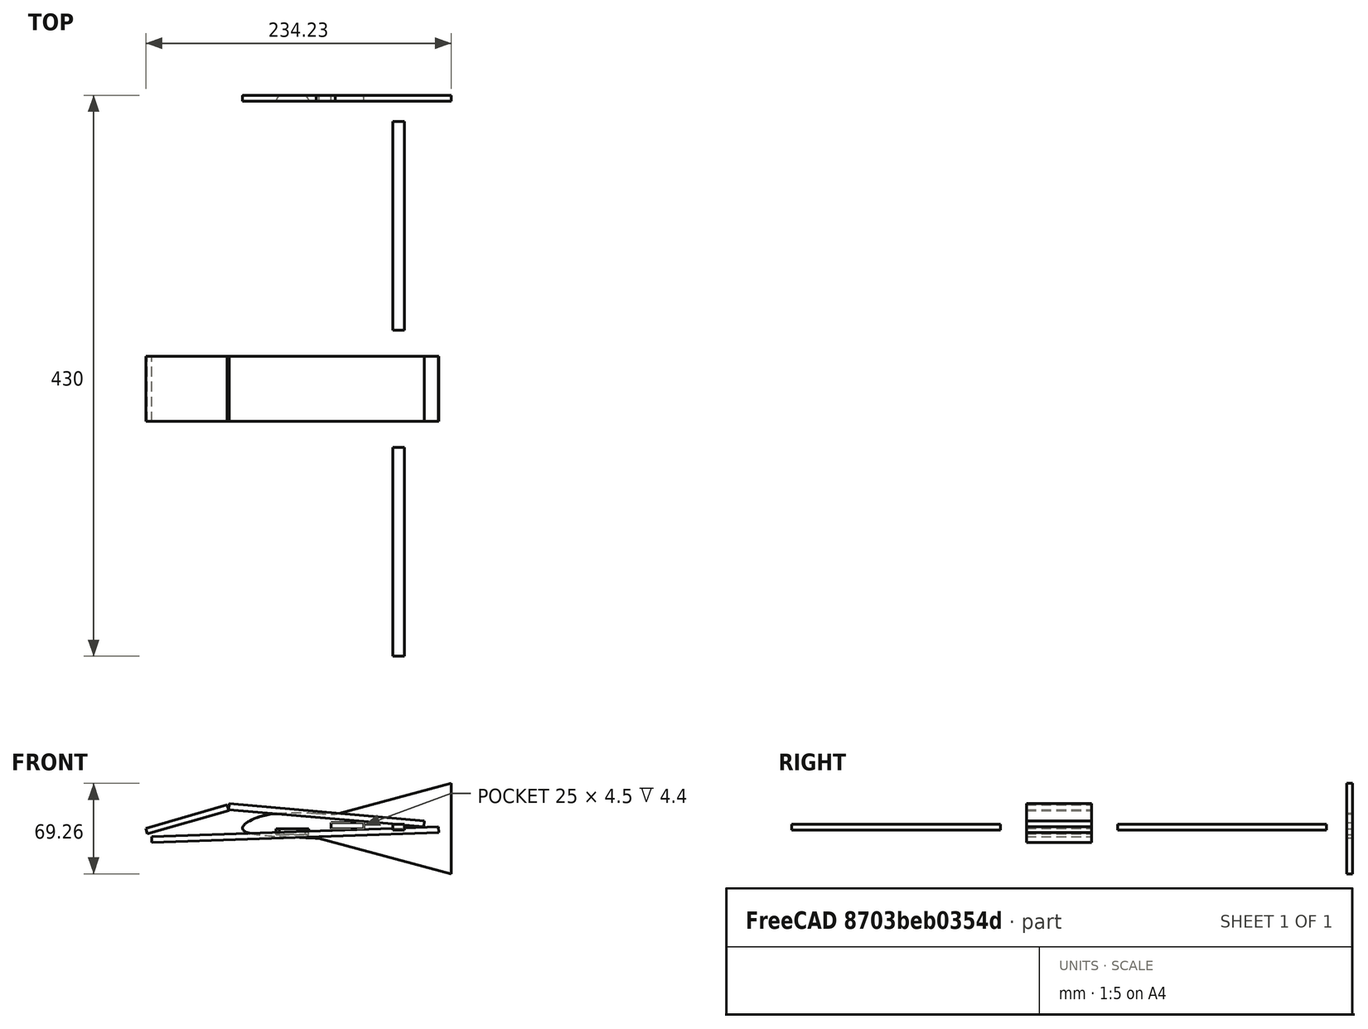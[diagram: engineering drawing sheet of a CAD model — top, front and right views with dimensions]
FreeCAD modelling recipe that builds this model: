
FCSTD DOCUMENT  (FreeCAD 0.21R33694 (Git))
Label: wingtest4
License: All rights reserved
LicenseURL: http://en.wikipedia.org/wiki/All_rights_reserved
objects: Part::FeaturePython×110, Part::Part2DObjectPython×22, Part::Box×9, Part::Cut×9, PartDesign::Body×8, Sketcher::SketchObject×6, PartDesign::FeatureBase×4, PartDesign::Pad×3, App::DocumentObjectGroup×3, Part::RuledSurface×2, Spreadsheet::Sheet×1, Part::Cylinder×1, Part::Fuse×1, App::FeaturePython×1, App::MeasureDistance×1, Part::MultiFuse×1, Mesh::Feature×1, Part::Feature×1
note: 181 computed .brp shape members not serialized (recipe doc carries the construction recipe); baked Part::Feature solids carry a one-line shape summary decoded from their .brp

FEATURE [Part::FeaturePython] wrib  # WARN: FeaturePython — macro-defined, semantics opaque (R4)
  Chord = 250
  Coordinates = (101) [(1,0,-1.66492e-17),(0.99901,0,0.000165389),(0.996045,0,0.000659808),(0.991115,0,0.00147806),(0.984241,0,0.00261162),(0.97545,0,0.00404888),+95 more]
  NacaNbrPoint = 50
  NacaProfil = 24112
  RibProfil = 24112
  Thickness = 0
  finite_TE = false
  splitSpline = true
  useSpline = true
  wingkey = 0
  expr: .Placement.Base.y = Spreadsheet.lw_start
FEATURE [Part::FeaturePython] wrib001  # WARN: FeaturePython — macro-defined, semantics opaque (R4)
  Chord = 250
  Coordinates = (101) [(1,0,-1.66492e-17),(0.99901,0,0.000165389),(0.996045,0,0.000659808),(0.991115,0,0.00147806),(0.984241,0,0.00261162),(0.97545,0,0.00404888),+95 more]
  NacaNbrPoint = 50
  NacaProfil = 24112
  Placement = pos=(0,50,0) rot=(1,0,0;0rad)
  RibProfil = 24112
  Thickness = 0
  finite_TE = false
  splitSpline = true
  useSpline = true
  wingkey = 0
  expr: .Placement.Base.y = Spreadsheet.rw_start
FEATURE [Part::FeaturePython] wrib002  # WARN: FeaturePython — macro-defined, semantics opaque (R4)
  Chord = 250
  Coordinates = (101) [(1,0,-1.66492e-17),(0.99901,0,0.000165389),(0.996045,0,0.000659808),(0.991115,0,0.00147806),(0.984241,0,0.00261162),(0.97545,0,0.00404888),+95 more]
  NacaNbrPoint = 50
  NacaProfil = 24112
  Placement = pos=(0,-40,0) rot=(1,0,0;0rad)
  RibProfil = 24112
  Thickness = 0
  finite_TE = false
  splitSpline = true
  useSpline = true
  wingkey = 0
  expr: .Placement.Base.y = Spreadsheet.lw_start - Spreadsheet.spacing * 2
FEATURE [Part::FeaturePython] wrib003  # WARN: FeaturePython — macro-defined, semantics opaque (R4)
  Chord = 250
  Coordinates = (101) [(1,0,-1.66492e-17),(0.99901,0,0.000165389),(0.996045,0,0.000659808),(0.991115,0,0.00147806),(0.984241,0,0.00261162),(0.97545,0,0.00404888),+95 more]
  NacaNbrPoint = 50
  NacaProfil = 24112
  Placement = pos=(0,-20,0) rot=(1,0,0;0rad)
  RibProfil = 24112
  Thickness = 0
  finite_TE = false
  splitSpline = true
  useSpline = true
  wingkey = 0
  expr: .Placement.Base.y = <<sht>>.lw_start - <<sht>>.spacing
FEATURE [Part::FeaturePython] wrib004  # WARN: FeaturePython — macro-defined, semantics opaque (R4)
  Chord = 250
  Coordinates = (101) [(1,0,-1.66492e-17),(0.99901,0,0.000165389),(0.996045,0,0.000659808),(0.991115,0,0.00147806),(0.984241,0,0.00261162),(0.97545,0,0.00404888),+95 more]
  NacaNbrPoint = 50
  NacaProfil = 24112
  Placement = pos=(0,70,0) rot=(1,0,0;0rad)
  RibProfil = 24112
  Thickness = 0
  finite_TE = false
  splitSpline = true
  useSpline = true
  wingkey = 0
  expr: .Placement.Base.y = Spreadsheet.rw_start + Spreadsheet.spacing
FEATURE [Part::FeaturePython] wrib005  # WARN: FeaturePython — macro-defined, semantics opaque (R4)
  Chord = 250
  Coordinates = (101) [(1,0,-1.66492e-17),(0.99901,0,0.000165389),(0.996045,0,0.000659808),(0.991115,0,0.00147806),(0.984241,0,0.00261162),(0.97545,0,0.00404888),+95 more]
  NacaNbrPoint = 50
  NacaProfil = 24112
  Placement = pos=(0,90,0) rot=(1,0,0;0rad)
  RibProfil = 24112
  Thickness = 0
  finite_TE = false
  splitSpline = true
  useSpline = true
  wingkey = 0
  expr: .Placement.Base.y = <<sht>>.rw_start + <<sht>>.spacing * 2
FEATURE [Spreadsheet::Sheet] Spreadsheet  label="sht"
  cells = A1='spacing; B1(spacing)=20; A2='lw_start; B2(lw_start)=0; A3='rw_start; B3(rw_start)=50; A4='wing_step; B4(wing_step)=15; A5='fb_spacing; B5(fb_spacing)=15; A6='thickness; B6(thickness)=4.5
FEATURE [Part::FeaturePython] wrib006  # WARN: FeaturePython — macro-defined, semantics opaque (R4)
  Chord = 235
  Coordinates = (101) [(1,0,-1.66492e-17),(0.99901,0,0.000165389),(0.996045,0,0.000659808),(0.991115,0,0.00147806),(0.984241,0,0.00261162),(0.97545,0,0.00404888),+95 more]
  NacaNbrPoint = 50
  NacaProfil = 24112
  Placement = pos=(15,-60,0) rot=(1,0,0;0rad)
  RibProfil = 24112
  Thickness = 0
  finite_TE = false
  splitSpline = true
  useSpline = true
  wingkey = 0
  expr: .Placement.Base.x = <<sht>>.fb_spacing
  expr: .Placement.Base.y = <<sht>>.lw_start - <<sht>>.spacing * 3
FEATURE [Part::FeaturePython] wrib007  # WARN: FeaturePython — macro-defined, semantics opaque (R4)
  Chord = 235
  Coordinates = (101) [(1,0,-1.66492e-17),(0.99901,0,0.000165389),(0.996045,0,0.000659808),(0.991115,0,0.00147806),(0.984241,0,0.00261162),(0.97545,0,0.00404888),+95 more]
  NacaNbrPoint = 50
  NacaProfil = 24112
  Placement = pos=(15,110,0) rot=(1,0,0;0rad)
  RibProfil = 24112
  Thickness = 0
  finite_TE = false
  splitSpline = true
  useSpline = true
  wingkey = 0
  expr: .Placement.Base.x = <<sht>>.fb_spacing
  expr: .Placement.Base.y = <<sht>>.rw_start + 3 * <<sht>>.spacing
FEATURE [Part::FeaturePython] wrib008  # WARN: FeaturePython — macro-defined, semantics opaque (R4)
  Chord = 220
  Coordinates = (101) [(1,0,-1.66492e-17),(0.99901,0,0.000165389),(0.996045,0,0.000659808),(0.991115,0,0.00147806),(0.984241,0,0.00261162),(0.97545,0,0.00404888),+95 more]
  NacaNbrPoint = 50
  NacaProfil = 24112
  Placement = pos=(30,-80,0) rot=(1,0,0;0rad)
  RibProfil = 24112
  Thickness = 0
  finite_TE = false
  splitSpline = true
  useSpline = true
  wingkey = 0
  expr: .Placement.Base.x = <<sht>>.fb_spacing * 2
  expr: .Placement.Base.y = <<sht>>.lw_start - <<sht>>.spacing * 4
FEATURE [Part::FeaturePython] wrib009  # WARN: FeaturePython — macro-defined, semantics opaque (R4)
  Chord = 220
  Coordinates = (101) [(1,0,-1.66492e-17),(0.99901,0,0.000165389),(0.996045,0,0.000659808),(0.991115,0,0.00147806),(0.984241,0,0.00261162),(0.97545,0,0.00404888),+95 more]
  NacaNbrPoint = 50
  NacaProfil = 24112
  Placement = pos=(30,130,0) rot=(1,0,0;0rad)
  RibProfil = 24112
  Thickness = 0
  finite_TE = false
  splitSpline = true
  useSpline = true
  wingkey = 0
  expr: .Placement.Base.x = <<sht>>.fb_spacing * 2
  expr: .Placement.Base.y = <<sht>>.rw_start + <<sht>>.spacing * 4
FEATURE [Part::FeaturePython] wrib010  # WARN: FeaturePython — macro-defined, semantics opaque (R4)
  Chord = 205
  Coordinates = (101) [(1,0,-1.66492e-17),(0.99901,0,0.000165389),(0.996045,0,0.000659808),(0.991115,0,0.00147806),(0.984241,0,0.00261162),(0.97545,0,0.00404888),+95 more]
  NacaNbrPoint = 50
  NacaProfil = 24112
  Placement = pos=(45,-100,0) rot=(1,0,0;0rad)
  RibProfil = 24112
  Thickness = 0
  finite_TE = false
  splitSpline = true
  useSpline = true
  wingkey = 0
  expr: .Placement.Base.x = <<sht>>.fb_spacing * 3
  expr: .Placement.Base.y = <<sht>>.lw_start - <<sht>>.spacing * 5
FEATURE [Part::FeaturePython] wrib011  # WARN: FeaturePython — macro-defined, semantics opaque (R4)
  Chord = 190
  Coordinates = (101) [(1,0,-1.66492e-17),(0.99901,0,0.000165389),(0.996045,0,0.000659808),(0.991115,0,0.00147806),(0.984241,0,0.00261162),(0.97545,0,0.00404888),+95 more]
  NacaNbrPoint = 50
  NacaProfil = 24112
  Placement = pos=(60,-120,0) rot=(1,0,0;0rad)
  RibProfil = 24112
  Thickness = 0
  finite_TE = false
  splitSpline = true
  useSpline = true
  wingkey = 0
  expr: .Placement.Base.x = <<sht>>.fb_spacing * 4
  expr: .Placement.Base.y = <<sht>>.lw_start - <<sht>>.spacing * 6
FEATURE [Part::FeaturePython] wrib012  # WARN: FeaturePython — macro-defined, semantics opaque (R4)
  Chord = 190
  Coordinates = (101) [(1,0,-1.66492e-17),(0.99901,0,0.000165389),(0.996045,0,0.000659808),(0.991115,0,0.00147806),(0.984241,0,0.00261162),(0.97545,0,0.00404888),+95 more]
  NacaNbrPoint = 50
  NacaProfil = 24112
  Placement = pos=(60,170,0) rot=(1,0,0;0rad)
  RibProfil = 24112
  Thickness = 0
  finite_TE = false
  splitSpline = true
  useSpline = true
  wingkey = 0
  expr: .Placement.Base.x = <<sht>>.fb_spacing * 4
  expr: .Placement.Base.y = <<sht>>.rw_start + <<sht>>.spacing * 6
FEATURE [Part::FeaturePython] wrib013  # WARN: FeaturePython — macro-defined, semantics opaque (R4)
  Chord = 205
  Coordinates = (101) [(1,0,-1.66492e-17),(0.99901,0,0.000165389),(0.996045,0,0.000659808),(0.991115,0,0.00147806),(0.984241,0,0.00261162),(0.97545,0,0.00404888),+95 more]
  NacaNbrPoint = 50
  NacaProfil = 24112
  Placement = pos=(45,150,0) rot=(1,0,0;0rad)
  RibProfil = 24112
  Thickness = 0
  finite_TE = false
  splitSpline = true
  useSpline = true
  wingkey = 0
  expr: .Placement.Base.x = <<sht>>.fb_spacing * 3
  expr: .Placement.Base.y = <<sht>>.rw_start + <<sht>>.spacing * 5
FEATURE [Part::FeaturePython] wrib014  # WARN: FeaturePython — macro-defined, semantics opaque (R4)
  Chord = 175
  Coordinates = (101) [(1,0,-1.66492e-17),(0.99901,0,0.000165389),(0.996045,0,0.000659808),(0.991115,0,0.00147806),(0.984241,0,0.00261162),(0.97545,0,0.00404888),+95 more]
  NacaNbrPoint = 50
  NacaProfil = 24112
  Placement = pos=(75,-140,0) rot=(1,0,0;0rad)
  RibProfil = 24112
  Thickness = 0
  finite_TE = false
  splitSpline = true
  useSpline = true
  wingkey = 0
  expr: .Placement.Base.x = <<sht>>.fb_spacing * 5
  expr: .Placement.Base.y = <<sht>>.lw_start - <<sht>>.spacing * 7
FEATURE [Part::FeaturePython] wrib015  # WARN: FeaturePython — macro-defined, semantics opaque (R4)
  Chord = 175
  Coordinates = (101) [(1,0,-1.66492e-17),(0.99901,0,0.000165389),(0.996045,0,0.000659808),(0.991115,0,0.00147806),(0.984241,0,0.00261162),(0.97545,0,0.00404888),+95 more]
  NacaNbrPoint = 50
  NacaProfil = 24112
  Placement = pos=(75,190,0) rot=(1,0,0;0rad)
  RibProfil = 24112
  Thickness = 0
  finite_TE = false
  splitSpline = true
  useSpline = true
  wingkey = 0
  expr: .Placement.Base.x = <<sht>>.fb_spacing * 5
  expr: .Placement.Base.y = <<sht>>.rw_start + <<sht>>.spacing * 7
FEATURE [Part::FeaturePython] wrib016  # WARN: FeaturePython — macro-defined, semantics opaque (R4)
  Chord = 160
  Coordinates = (101) [(1,0,-1.65073e-17),(0.999032,0,0.000273506),(0.996132,0,0.00109061),(0.99131,0,0.00244114),(0.984583,0,0.00430839),(0.975972,0,0.00666943),+95 more]
  NacaNbrPoint = 50
  NacaProfil = 4412
  Placement = pos=(90,210,0) rot=(1,0,0;0rad)
  RibProfil = 4412
  Thickness = 0
  finite_TE = false
  splitSpline = true
  useSpline = true
  wingkey = 0
  expr: .Placement.Base.x = <<sht>>.fb_spacing * 6
  expr: .Placement.Base.y = <<sht>>.rw_start + <<sht>>.spacing * 8
FEATURE [Part::FeaturePython] wrib017  # WARN: FeaturePython — macro-defined, semantics opaque (R4)
  Chord = 160
  Coordinates = (101) [(1,0,-1.66492e-17),(0.99901,0,0.000165389),(0.996045,0,0.000659808),(0.991115,0,0.00147806),(0.984241,0,0.00261162),(0.97545,0,0.00404888),+95 more]
  NacaNbrPoint = 50
  NacaProfil = 24112
  Placement = pos=(90,-160,0) rot=(1,0,0;0rad)
  RibProfil = 24112
  Thickness = 0
  finite_TE = false
  splitSpline = true
  useSpline = true
  wingkey = 0
  expr: .Placement.Base.x = <<sht>>.fb_spacing * 6
  expr: .Placement.Base.y = <<sht>>.lw_start - <<sht>>.spacing * 8
FEATURE [Part::FeaturePython] wrib018  # WARN: FeaturePython — macro-defined, semantics opaque (R4)
  Chord = 160
  Coordinates = (101) [(1,0,-1.66492e-17),(0.99901,0,0.000165389),(0.996045,0,0.000659808),(0.991115,0,0.00147806),(0.984241,0,0.00261162),(0.97545,0,0.00404888),+95 more]
  NacaNbrPoint = 50
  NacaProfil = 24112
  Placement = pos=(90,-180,0) rot=(1,0,0;0rad)
  RibProfil = 24112
  Thickness = 0
  finite_TE = false
  splitSpline = true
  useSpline = true
  wingkey = 0
  expr: .Placement.Base.x = <<sht>>.fb_spacing * 6
  expr: .Placement.Base.y = <<sht>>.lw_start - <<sht>>.spacing * 9
FEATURE [Part::FeaturePython] wrib019  # WARN: FeaturePython — macro-defined, semantics opaque (R4)
  Chord = 160
  Coordinates = (101) [(1,0,-1.66492e-17),(0.99901,0,0.000165389),(0.996045,0,0.000659808),(0.991115,0,0.00147806),(0.984241,0,0.00261162),(0.97545,0,0.00404888),+95 more]
  NacaNbrPoint = 50
  NacaProfil = 24112
  Placement = pos=(90,-200,0) rot=(1,0,0;0rad)
  RibProfil = 24112
  Thickness = 0
  finite_TE = false
  splitSpline = true
  useSpline = true
  wingkey = 0
  expr: .Placement.Base.x = <<sht>>.fb_spacing * 6
  expr: .Placement.Base.y = <<sht>>.lw_start - <<sht>>.spacing * 10
FEATURE [Part::FeaturePython] wrib020  # WARN: FeaturePython — macro-defined, semantics opaque (R4)
  Chord = 160
  Coordinates = (101) [(1,0,-1.66492e-17),(0.99901,0,0.000165389),(0.996045,0,0.000659808),(0.991115,0,0.00147806),(0.984241,0,0.00261162),(0.97545,0,0.00404888),+95 more]
  NacaNbrPoint = 50
  NacaProfil = 24112
  Placement = pos=(90,230,0) rot=(1,0,0;0rad)
  RibProfil = 24112
  Thickness = 0
  finite_TE = false
  splitSpline = true
  useSpline = true
  wingkey = 0
  expr: .Placement.Base.x = <<sht>>.fb_spacing * 6
  expr: .Placement.Base.y = <<sht>>.rw_start + <<sht>>.spacing * 9
FEATURE [Part::FeaturePython] wrib021  # WARN: FeaturePython — macro-defined, semantics opaque (R4)
  Chord = 160
  Coordinates = (101) [(1,0,-1.66492e-17),(0.99901,0,0.000165389),(0.996045,0,0.000659808),(0.991115,0,0.00147806),(0.984241,0,0.00261162),(0.97545,0,0.00404888),+95 more]
  NacaNbrPoint = 50
  NacaProfil = 24112
  Placement = pos=(90,250,0) rot=(1,0,0;0rad)
  RibProfil = 24112
  Thickness = 0
  finite_TE = false
  splitSpline = true
  useSpline = true
  wingkey = 0
  expr: .Placement.Base.x = <<sht>>.fb_spacing * 6
  expr: .Placement.Base.y = <<sht>>.rw_start + <<sht>>.spacing * 10
FEATURE [Sketcher::SketchObject] Sketch
  FullyConstrained = false
  MapMode = 5
  Placement = pos=(0,0,0) rot=(1,0,0;1.5708rad)
  Support = -> [XZ_Plane]
  sketch-geometry (29):
    g0: LineSegment StartX=0 StartY=34.6308 StartZ=0 EndX=0 EndY=-34.6308 EndZ=0
    g1: LineSegment StartX=0 StartY=-34.6308 StartZ=0 EndX=-101.691 EndY=-7.38276 EndZ=0
    g2-g12: Circle x11 (B-spline internal-alignment scaffolding for g13; pole/knot coordinates omitted)
    g13: BSplineCurve PolesCount=11 KnotsCount=9 Degree=3 IsPeriodic=0
    g14: GeomPoint X=-103.524 Y=11.6623 Z=0
    g15: GeomPoint X=-140.833 Y=10.5678 Z=0
    g16: GeomPoint X=-152.621 Y=6.9811 Z=0
    g17: GeomPoint X=-158.306 Y=3.35011 Z=0
    g18: GeomPoint X=-160.007 Y=0.321331 Z=0
    g19: GeomPoint X=-158.483 Y=-2.12294 Z=0
    g20: GeomPoint X=-153.453 Y=-3.75246 Z=0
    g21: GeomPoint X=-144.695 Y=-5.06316 Z=0
    g22: GeomPoint X=-101.691 Y=-7.38276 Z=0
    g23: LineSegment StartX=-88.9876 StartY=10.9761 StartZ=0 EndX=0 EndY=34.6308 EndZ=0
    g24: Circle CenterX=-103.524 CenterY=11.6623 CenterZ=0 NormalX=0 NormalY=0 NormalZ=1 AngleXU=0 Radius=1
    g25: Circle CenterX=-88.9876 CenterY=10.9761 CenterZ=0 NormalX=0 NormalY=0 NormalZ=1 AngleXU=0 Radius=1
    g26: BSplineCurve PolesCount=2 KnotsCount=2 Degree=1 IsPeriodic=0
    g27: GeomPoint X=-103.524 Y=11.6623 Z=0
    g28: GeomPoint X=-88.9876 Y=10.9761 Z=0
  constraints (8):
    c: PointOnObject(g0,g-2)
    c: Coincident(g0,g1)
    c: Coincident(g23,g0)
    c: Symmetric(g0,g0,g-1)
    c: Weight(g2) = 1
    c: Equal(g2, g3-g12) x10
    c: Coincident(g13,g1)
    c: InternalAlignment(g2-g12 -> g13) x11
FEATURE [PartDesign::Pad] Pad
  Direction = (0,-1,2e-16)
  Length = 4.5
  Length2 = 10
  Placement = pos=(0,0,0) rot=(1,0,0;1.5708rad)
  Profile = -> Sketch
  ReferenceAxis = -> Sketch [N_Axis]
  Type = 0
  expr: Length = <<sht>>.thickness
FEATURE [PartDesign::Body] Body  label="wingtip1"
  Group = -> [Sketch,Pad]
  Origin = -> Origin
  Placement = pos=(250,250,0) rot=(0,0,1;0rad)
  Tip = -> Pad
  expr: .Placement.Base.x = <<sht>>.fb_spacing * 6 mm + wrib021.Chord
FEATURE [PartDesign::FeatureBase] Clone
  BaseFeature = -> Body
  Placement = pos=(250,250,0) rot=(0,0,1;0rad)
FEATURE [PartDesign::Body] Body001  label="wingtip2"
  BaseFeature = -> Body
  Group = -> [Clone]
  Origin = -> Origin001
  Placement = pos=(0,-449.2,0) rot=(0,0,1;0rad)
  Tip = -> Clone
  expr: .Placement.Base.y = 0
FEATURE [Sketcher::SketchObject] Sketch001
  FullyConstrained = false
  MapMode = 5
  Support = -> [XY_Plane002]
  sketch-geometry (51):
    g0-g25: Circle x26 (B-spline internal-alignment scaffolding for g26; pole/knot coordinates omitted)
    g26: BSplineCurve PolesCount=26 KnotsCount=24 Degree=3 IsPeriodic=0
    g27-g50: GeomPoint x24 (B-spline internal-alignment scaffolding for g26; pole/knot coordinates omitted)
  constraints (5):
    c: Weight(g0) = 1
    c: Equal(g0, g1-g25) x25
    c: Coincident(g26,g0)
    c: InternalAlignment(g0-g25 -> g26) x26
    c: InternalAlignment(g27-g50 -> g26) x24
FEATURE [PartDesign::Pad] Pad001
  Direction = (0,0,1)
  Length = 4.5
  Length2 = 10
  Profile = -> Sketch001
  ReferenceAxis = -> Sketch001 [N_Axis]
  Type = 0
  expr: Length = <<sht>>.thickness
FEATURE [PartDesign::Body] Body002  label="flexspar"
  Group = -> [Sketch001,Pad001]
  Origin = -> Origin002
  Tip = -> Pad001
FEATURE [PartDesign::FeatureBase] Clone001
  BaseFeature = -> Body002
FEATURE [PartDesign::Body] Body003
  BaseFeature = -> Body002
  Group = -> [Clone001]
  Origin = -> Origin003
  Placement = pos=(0,46.93,1e-15) rot=(1,0,0;3.14159rad)
  Tip = -> Clone001
FEATURE [Part::Box] Box  label="Cube"
  AttacherType = Attacher::AttachEngine3D
  Height = 20
  Length = 45
  Placement = pos=(210,-170,-9) rot=(0,0,1;0rad)
  Width = 141
  expr: .Placement.Base.x = 210
FEATURE [Part::FeaturePython] BooleanFragments  # WARN: FeaturePython — macro-defined, semantics opaque (R4)
  Mode = 0
  Objects = -> [wrib,wrib001,wrib002,wrib003,wrib004,wrib005,wrib006,wrib007,wrib008,wrib009,wrib010,wrib011,wrib012,wrib013,wrib014,wrib015,wrib016,wrib017,wrib018,wrib019,wrib020,wrib021,Body,Body001]
  Tolerance = 0
FEATURE [Part::Cylinder] Cylinder
  Angle = 360
  AttacherType = Attacher::AttachEngine3D
  FirstAngle = 0
  Height = 140
  Placement = pos=(210,-30,0.03) rot=(0.999938,0,0.01111;1.5708rad)
  Radius = 11
  SecondAngle = 0
FEATURE [Part::Fuse] Fusion
  Base = -> Box
  Tool = -> Cylinder
FEATURE [PartDesign::FeatureBase] Clone002
  BaseFeature = -> Fusion
FEATURE [PartDesign::Body] Body004
  BaseFeature = -> Fusion
  Group = -> [Clone002]
  Origin = -> Origin004
  Placement = pos=(0,253.5,0) rot=(0,0,1;0rad)
  Tip = -> Clone002
FEATURE [Part::FeaturePython] BooleanFragments001  # WARN: FeaturePython — macro-defined, semantics opaque (R4)
  Mode = 0
  Objects = -> [Body004,Fusion]
  Tolerance = 0
FEATURE [Part::Box] Box001  label="Cube001"
  AttacherType = Attacher::AttachEngine3D
  Height = 100
  Length = 340
  Placement = pos=(-1,-260,-49) rot=(0,0,1;0rad)
  Width = 550
FEATURE [Part::FeaturePython] BooleanFragments001_child0  label="BooleanFragments001.0"  # WARN: FeaturePython — macro-defined, semantics opaque (R4)
  Base = -> BooleanFragments001
  FilterType = 1
  Invert = false
  OverrideMaxVal = 0
  WindowFrom = 80
  WindowTo = 100
  items = 0
FEATURE [Part::FeaturePython] BooleanFragments001_child1  label="BooleanFragments001.1"  # WARN: FeaturePython — macro-defined, semantics opaque (R4)
  Base = -> BooleanFragments001
  FilterType = 1
  Invert = false
  OverrideMaxVal = 0
  WindowFrom = 80
  WindowTo = 100
  items = 1
FEATURE [Sketcher::SketchObject] Sketch002
  FullyConstrained = false
  MapMode = 5
  Placement = pos=(0,0,0) rot=(1,0,0;1.5708rad)
  Support = -> [XZ_Plane005]
  sketch-geometry (29):
    g0: LineSegment StartX=0 StartY=34.6308 StartZ=0 EndX=0 EndY=-34.6308 EndZ=0
    g1: LineSegment StartX=0 StartY=-34.6308 StartZ=0 EndX=-101.691 EndY=-7.38276 EndZ=0
    g2-g12: Circle x11 (B-spline internal-alignment scaffolding for g13; pole/knot coordinates omitted)
    g13: BSplineCurve PolesCount=11 KnotsCount=9 Degree=3 IsPeriodic=0
    g14: GeomPoint X=-103.524 Y=11.6623 Z=0
    g15: GeomPoint X=-140.833 Y=10.5678 Z=0
    g16: GeomPoint X=-152.621 Y=6.9811 Z=0
    g17: GeomPoint X=-158.306 Y=3.35011 Z=0
    g18: GeomPoint X=-160.007 Y=0.321331 Z=0
    g19: GeomPoint X=-158.483 Y=-2.12294 Z=0
    g20: GeomPoint X=-153.453 Y=-3.75246 Z=0
    g21: GeomPoint X=-144.695 Y=-5.06316 Z=0
    g22: GeomPoint X=-101.691 Y=-7.38276 Z=0
    g23: LineSegment StartX=-88.9876 StartY=10.9761 StartZ=0 EndX=0 EndY=34.6308 EndZ=0
    g24: Circle CenterX=-103.524 CenterY=11.6623 CenterZ=0 NormalX=0 NormalY=0 NormalZ=1 AngleXU=0 Radius=1
    g25: Circle CenterX=-88.9876 CenterY=10.9761 CenterZ=0 NormalX=0 NormalY=0 NormalZ=1 AngleXU=0 Radius=1
    g26: BSplineCurve PolesCount=2 KnotsCount=2 Degree=1 IsPeriodic=0
    g27: GeomPoint X=-103.524 Y=11.6623 Z=0
    g28: GeomPoint X=-88.9876 Y=10.9761 Z=0
  constraints (8):
    c: PointOnObject(g0,g-2)
    c: Coincident(g0,g1)
    c: Coincident(g23,g0)
    c: Symmetric(g0,g0,g-1)
    c: Weight(g2) = 1
    c: Equal(g2, g3-g12) x10
    c: Coincident(g13,g1)
    c: InternalAlignment(g2-g12 -> g13) x11
FEATURE [PartDesign::Pad] Pad002
  Direction = (0,-1,2e-16)
  Length = 4.5
  Length2 = 10
  Placement = pos=(0,0,0) rot=(1,0,0;1.5708rad)
  Profile = -> Sketch002
  ReferenceAxis = -> Sketch002 [N_Axis]
  Type = 0
  expr: Length = <<sht>>.thickness
FEATURE [PartDesign::Body] Body005  label="wingtip003"
  Group = -> [Sketch002,Pad002]
  Origin = -> Origin005
  Placement = pos=(250,250,0) rot=(0,0,1;0rad)
  Tip = -> Pad002
  expr: .Placement.Base.x = <<sht>>.fb_spacing * 6 mm + wrib043.Chord
FEATURE [PartDesign::FeatureBase] Clone003
  BaseFeature = -> Body005
  Placement = pos=(250,250,0) rot=(0,0,1;0rad)
FEATURE [PartDesign::Body] Body006  label="wingtip004"
  BaseFeature = -> Body005
  Group = -> [Clone003]
  Origin = -> Origin006
  Placement = pos=(0,-449.2,0) rot=(0,0,1;0rad)
  Tip = -> Clone003
  expr: .Placement.Base.y = 0
FEATURE [Part::FeaturePython] wrib022  # WARN: FeaturePython — macro-defined, semantics opaque (R4)
  Chord = 250
  Coordinates = (101) [(1,0,-1.66492e-17),(0.99901,0,0.000165389),(0.996045,0,0.000659808),(0.991115,0,0.00147806),(0.984241,0,0.00261162),(0.97545,0,0.00404888),+95 more]
  NacaNbrPoint = 50
  NacaProfil = 24112
  RibProfil = 24112
  Thickness = 0
  finite_TE = false
  splitSpline = true
  useSpline = true
  wingkey = 0
  expr: .Placement.Base.y = Spreadsheet.lw_start
FEATURE [Part::FeaturePython] wrib023  # WARN: FeaturePython — macro-defined, semantics opaque (R4)
  Chord = 250
  Coordinates = (101) [(1,0,-1.66492e-17),(0.99901,0,0.000165389),(0.996045,0,0.000659808),(0.991115,0,0.00147806),(0.984241,0,0.00261162),(0.97545,0,0.00404888),+95 more]
  NacaNbrPoint = 50
  NacaProfil = 24112
  Placement = pos=(0,50,0) rot=(1,0,0;0rad)
  RibProfil = 24112
  Thickness = 0
  finite_TE = false
  splitSpline = true
  useSpline = true
  wingkey = 0
  expr: .Placement.Base.y = Spreadsheet.rw_start
FEATURE [Part::FeaturePython] wrib024  # WARN: FeaturePython — macro-defined, semantics opaque (R4)
  Chord = 250
  Coordinates = (101) [(1,0,-1.66492e-17),(0.99901,0,0.000165389),(0.996045,0,0.000659808),(0.991115,0,0.00147806),(0.984241,0,0.00261162),(0.97545,0,0.00404888),+95 more]
  NacaNbrPoint = 50
  NacaProfil = 24112
  Placement = pos=(0,-40,0) rot=(1,0,0;0rad)
  RibProfil = 24112
  Thickness = 0
  finite_TE = false
  splitSpline = true
  useSpline = true
  wingkey = 0
  expr: .Placement.Base.y = Spreadsheet.lw_start - Spreadsheet.spacing * 2
FEATURE [Part::FeaturePython] wrib025  # WARN: FeaturePython — macro-defined, semantics opaque (R4)
  Chord = 250
  Coordinates = (101) [(1,0,-1.66492e-17),(0.99901,0,0.000165389),(0.996045,0,0.000659808),(0.991115,0,0.00147806),(0.984241,0,0.00261162),(0.97545,0,0.00404888),+95 more]
  NacaNbrPoint = 50
  NacaProfil = 24112
  Placement = pos=(0,-20,0) rot=(1,0,0;0rad)
  RibProfil = 24112
  Thickness = 0
  finite_TE = false
  splitSpline = true
  useSpline = true
  wingkey = 0
  expr: .Placement.Base.y = <<sht>>.lw_start - <<sht>>.spacing
FEATURE [Part::FeaturePython] wrib026  # WARN: FeaturePython — macro-defined, semantics opaque (R4)
  Chord = 250
  Coordinates = (101) [(1,0,-1.66492e-17),(0.99901,0,0.000165389),(0.996045,0,0.000659808),(0.991115,0,0.00147806),(0.984241,0,0.00261162),(0.97545,0,0.00404888),+95 more]
  NacaNbrPoint = 50
  NacaProfil = 24112
  Placement = pos=(0,70,0) rot=(1,0,0;0rad)
  RibProfil = 24112
  Thickness = 0
  finite_TE = false
  splitSpline = true
  useSpline = true
  wingkey = 0
  expr: .Placement.Base.y = Spreadsheet.rw_start + Spreadsheet.spacing
FEATURE [Part::FeaturePython] wrib027  # WARN: FeaturePython — macro-defined, semantics opaque (R4)
  Chord = 250
  Coordinates = (101) [(1,0,-1.66492e-17),(0.99901,0,0.000165389),(0.996045,0,0.000659808),(0.991115,0,0.00147806),(0.984241,0,0.00261162),(0.97545,0,0.00404888),+95 more]
  NacaNbrPoint = 50
  NacaProfil = 24112
  Placement = pos=(0,90,0) rot=(1,0,0;0rad)
  RibProfil = 24112
  Thickness = 0
  finite_TE = false
  splitSpline = true
  useSpline = true
  wingkey = 0
  expr: .Placement.Base.y = <<sht>>.rw_start + <<sht>>.spacing * 2
FEATURE [Part::FeaturePython] wrib028  # WARN: FeaturePython — macro-defined, semantics opaque (R4)
  Chord = 235
  Coordinates = (101) [(1,0,-1.66492e-17),(0.99901,0,0.000165389),(0.996045,0,0.000659808),(0.991115,0,0.00147806),(0.984241,0,0.00261162),(0.97545,0,0.00404888),+95 more]
  NacaNbrPoint = 50
  NacaProfil = 24112
  Placement = pos=(15,-60,0) rot=(1,0,0;0rad)
  RibProfil = 24112
  Thickness = 0
  finite_TE = false
  splitSpline = true
  useSpline = true
  wingkey = 0
  expr: .Placement.Base.x = <<sht>>.fb_spacing
  expr: .Placement.Base.y = <<sht>>.lw_start - <<sht>>.spacing * 3
FEATURE [Part::FeaturePython] wrib029  # WARN: FeaturePython — macro-defined, semantics opaque (R4)
  Chord = 235
  Coordinates = (101) [(1,0,-1.66492e-17),(0.99901,0,0.000165389),(0.996045,0,0.000659808),(0.991115,0,0.00147806),(0.984241,0,0.00261162),(0.97545,0,0.00404888),+95 more]
  NacaNbrPoint = 50
  NacaProfil = 24112
  Placement = pos=(15,110,0) rot=(1,0,0;0rad)
  RibProfil = 24112
  Thickness = 0
  finite_TE = false
  splitSpline = true
  useSpline = true
  wingkey = 0
  expr: .Placement.Base.x = <<sht>>.fb_spacing
  expr: .Placement.Base.y = <<sht>>.rw_start + 3 * <<sht>>.spacing
FEATURE [Part::FeaturePython] wrib030  # WARN: FeaturePython — macro-defined, semantics opaque (R4)
  Chord = 220
  Coordinates = (101) [(1,0,-1.66492e-17),(0.99901,0,0.000165389),(0.996045,0,0.000659808),(0.991115,0,0.00147806),(0.984241,0,0.00261162),(0.97545,0,0.00404888),+95 more]
  NacaNbrPoint = 50
  NacaProfil = 24112
  Placement = pos=(30,-80,0) rot=(1,0,0;0rad)
  RibProfil = 24112
  Thickness = 0
  finite_TE = false
  splitSpline = true
  useSpline = true
  wingkey = 0
  expr: .Placement.Base.x = <<sht>>.fb_spacing * 2
  expr: .Placement.Base.y = <<sht>>.lw_start - <<sht>>.spacing * 4
FEATURE [Part::FeaturePython] wrib031  # WARN: FeaturePython — macro-defined, semantics opaque (R4)
  Chord = 220
  Coordinates = (101) [(1,0,-1.66492e-17),(0.99901,0,0.000165389),(0.996045,0,0.000659808),(0.991115,0,0.00147806),(0.984241,0,0.00261162),(0.97545,0,0.00404888),+95 more]
  NacaNbrPoint = 50
  NacaProfil = 24112
  Placement = pos=(30,130,0) rot=(1,0,0;0rad)
  RibProfil = 24112
  Thickness = 0
  finite_TE = false
  splitSpline = true
  useSpline = true
  wingkey = 0
  expr: .Placement.Base.x = <<sht>>.fb_spacing * 2
  expr: .Placement.Base.y = <<sht>>.rw_start + <<sht>>.spacing * 4
FEATURE [Part::FeaturePython] wrib032  # WARN: FeaturePython — macro-defined, semantics opaque (R4)
  Chord = 205
  Coordinates = (101) [(1,0,-1.66492e-17),(0.99901,0,0.000165389),(0.996045,0,0.000659808),(0.991115,0,0.00147806),(0.984241,0,0.00261162),(0.97545,0,0.00404888),+95 more]
  NacaNbrPoint = 50
  NacaProfil = 24112
  Placement = pos=(45,-100,0) rot=(1,0,0;0rad)
  RibProfil = 24112
  Thickness = 0
  finite_TE = false
  splitSpline = true
  useSpline = true
  wingkey = 0
  expr: .Placement.Base.x = <<sht>>.fb_spacing * 3
  expr: .Placement.Base.y = <<sht>>.lw_start - <<sht>>.spacing * 5
FEATURE [Part::FeaturePython] wrib033  # WARN: FeaturePython — macro-defined, semantics opaque (R4)
  Chord = 190
  Coordinates = (101) [(1,0,-1.66492e-17),(0.99901,0,0.000165389),(0.996045,0,0.000659808),(0.991115,0,0.00147806),(0.984241,0,0.00261162),(0.97545,0,0.00404888),+95 more]
  NacaNbrPoint = 50
  NacaProfil = 24112
  Placement = pos=(60,-120,0) rot=(1,0,0;0rad)
  RibProfil = 24112
  Thickness = 0
  finite_TE = false
  splitSpline = true
  useSpline = true
  wingkey = 0
  expr: .Placement.Base.x = <<sht>>.fb_spacing * 4
  expr: .Placement.Base.y = <<sht>>.lw_start - <<sht>>.spacing * 6
FEATURE [Part::FeaturePython] wrib034  # WARN: FeaturePython — macro-defined, semantics opaque (R4)
  Chord = 190
  Coordinates = (101) [(1,0,-1.66492e-17),(0.99901,0,0.000165389),(0.996045,0,0.000659808),(0.991115,0,0.00147806),(0.984241,0,0.00261162),(0.97545,0,0.00404888),+95 more]
  NacaNbrPoint = 50
  NacaProfil = 24112
  Placement = pos=(60,170,0) rot=(1,0,0;0rad)
  RibProfil = 24112
  Thickness = 0
  finite_TE = false
  splitSpline = true
  useSpline = true
  wingkey = 0
  expr: .Placement.Base.x = <<sht>>.fb_spacing * 4
  expr: .Placement.Base.y = <<sht>>.rw_start + <<sht>>.spacing * 6
FEATURE [Part::FeaturePython] wrib035  # WARN: FeaturePython — macro-defined, semantics opaque (R4)
  Chord = 205
  Coordinates = (101) [(1,0,-1.66492e-17),(0.99901,0,0.000165389),(0.996045,0,0.000659808),(0.991115,0,0.00147806),(0.984241,0,0.00261162),(0.97545,0,0.00404888),+95 more]
  NacaNbrPoint = 50
  NacaProfil = 24112
  Placement = pos=(45,150,0) rot=(1,0,0;0rad)
  RibProfil = 24112
  Thickness = 0
  finite_TE = false
  splitSpline = true
  useSpline = true
  wingkey = 0
  expr: .Placement.Base.x = <<sht>>.fb_spacing * 3
  expr: .Placement.Base.y = <<sht>>.rw_start + <<sht>>.spacing * 5
FEATURE [Part::FeaturePython] wrib036  # WARN: FeaturePython — macro-defined, semantics opaque (R4)
  Chord = 175
  Coordinates = (101) [(1,0,-1.66492e-17),(0.99901,0,0.000165389),(0.996045,0,0.000659808),(0.991115,0,0.00147806),(0.984241,0,0.00261162),(0.97545,0,0.00404888),+95 more]
  NacaNbrPoint = 50
  NacaProfil = 24112
  Placement = pos=(75,-140,0) rot=(1,0,0;0rad)
  RibProfil = 24112
  Thickness = 0
  finite_TE = false
  splitSpline = true
  useSpline = true
  wingkey = 0
  expr: .Placement.Base.x = <<sht>>.fb_spacing * 5
  expr: .Placement.Base.y = <<sht>>.lw_start - <<sht>>.spacing * 7
FEATURE [Part::FeaturePython] wrib037  # WARN: FeaturePython — macro-defined, semantics opaque (R4)
  Chord = 175
  Coordinates = (101) [(1,0,-1.66492e-17),(0.99901,0,0.000165389),(0.996045,0,0.000659808),(0.991115,0,0.00147806),(0.984241,0,0.00261162),(0.97545,0,0.00404888),+95 more]
  NacaNbrPoint = 50
  NacaProfil = 24112
  Placement = pos=(75,190,0) rot=(1,0,0;0rad)
  RibProfil = 24112
  Thickness = 0
  finite_TE = false
  splitSpline = true
  useSpline = true
  wingkey = 0
  expr: .Placement.Base.x = <<sht>>.fb_spacing * 5
  expr: .Placement.Base.y = <<sht>>.rw_start + <<sht>>.spacing * 7
FEATURE [Part::FeaturePython] wrib038  # WARN: FeaturePython — macro-defined, semantics opaque (R4)
  Chord = 160
  Coordinates = (101) [(1,0,-1.65073e-17),(0.999032,0,0.000273506),(0.996132,0,0.00109061),(0.99131,0,0.00244114),(0.984583,0,0.00430839),(0.975972,0,0.00666943),+95 more]
  NacaNbrPoint = 50
  NacaProfil = 4412
  Placement = pos=(90,210,0) rot=(1,0,0;0rad)
  RibProfil = 4412
  Thickness = 0
  finite_TE = false
  splitSpline = true
  useSpline = true
  wingkey = 0
  expr: .Placement.Base.x = <<sht>>.fb_spacing * 6
  expr: .Placement.Base.y = <<sht>>.rw_start + <<sht>>.spacing * 8
FEATURE [Part::FeaturePython] wrib039  # WARN: FeaturePython — macro-defined, semantics opaque (R4)
  Chord = 160
  Coordinates = (101) [(1,0,-1.66492e-17),(0.99901,0,0.000165389),(0.996045,0,0.000659808),(0.991115,0,0.00147806),(0.984241,0,0.00261162),(0.97545,0,0.00404888),+95 more]
  NacaNbrPoint = 50
  NacaProfil = 24112
  Placement = pos=(90,-160,0) rot=(1,0,0;0rad)
  RibProfil = 24112
  Thickness = 0
  finite_TE = false
  splitSpline = true
  useSpline = true
  wingkey = 0
  expr: .Placement.Base.x = <<sht>>.fb_spacing * 6
  expr: .Placement.Base.y = <<sht>>.lw_start - <<sht>>.spacing * 8
FEATURE [Part::FeaturePython] wrib040  # WARN: FeaturePython — macro-defined, semantics opaque (R4)
  Chord = 160
  Coordinates = (101) [(1,0,-1.66492e-17),(0.99901,0,0.000165389),(0.996045,0,0.000659808),(0.991115,0,0.00147806),(0.984241,0,0.00261162),(0.97545,0,0.00404888),+95 more]
  NacaNbrPoint = 50
  NacaProfil = 24112
  Placement = pos=(90,-180,0) rot=(1,0,0;0rad)
  RibProfil = 24112
  Thickness = 0
  finite_TE = false
  splitSpline = true
  useSpline = true
  wingkey = 0
  expr: .Placement.Base.x = <<sht>>.fb_spacing * 6
  expr: .Placement.Base.y = <<sht>>.lw_start - <<sht>>.spacing * 9
FEATURE [Part::FeaturePython] wrib041  # WARN: FeaturePython — macro-defined, semantics opaque (R4)
  Chord = 160
  Coordinates = (101) [(1,0,-1.66492e-17),(0.99901,0,0.000165389),(0.996045,0,0.000659808),(0.991115,0,0.00147806),(0.984241,0,0.00261162),(0.97545,0,0.00404888),+95 more]
  NacaNbrPoint = 50
  NacaProfil = 24112
  Placement = pos=(90,-200,0) rot=(1,0,0;0rad)
  RibProfil = 24112
  Thickness = 0
  finite_TE = false
  splitSpline = true
  useSpline = true
  wingkey = 0
  expr: .Placement.Base.x = <<sht>>.fb_spacing * 6
  expr: .Placement.Base.y = <<sht>>.lw_start - <<sht>>.spacing * 10
FEATURE [Part::FeaturePython] wrib042  # WARN: FeaturePython — macro-defined, semantics opaque (R4)
  Chord = 160
  Coordinates = (101) [(1,0,-1.66492e-17),(0.99901,0,0.000165389),(0.996045,0,0.000659808),(0.991115,0,0.00147806),(0.984241,0,0.00261162),(0.97545,0,0.00404888),+95 more]
  NacaNbrPoint = 50
  NacaProfil = 24112
  Placement = pos=(90,230,0) rot=(1,0,0;0rad)
  RibProfil = 24112
  Thickness = 0
  finite_TE = false
  splitSpline = true
  useSpline = true
  wingkey = 0
  expr: .Placement.Base.x = <<sht>>.fb_spacing * 6
  expr: .Placement.Base.y = <<sht>>.rw_start + <<sht>>.spacing * 9
FEATURE [Part::FeaturePython] wrib043  # WARN: FeaturePython — macro-defined, semantics opaque (R4)
  Chord = 160
  Coordinates = (101) [(1,0,-1.66492e-17),(0.99901,0,0.000165389),(0.996045,0,0.000659808),(0.991115,0,0.00147806),(0.984241,0,0.00261162),(0.97545,0,0.00404888),+95 more]
  NacaNbrPoint = 50
  NacaProfil = 24112
  Placement = pos=(90,250,0) rot=(1,0,0;0rad)
  RibProfil = 24112
  Thickness = 0
  finite_TE = false
  splitSpline = true
  useSpline = true
  wingkey = 0
  expr: .Placement.Base.x = <<sht>>.fb_spacing * 6
  expr: .Placement.Base.y = <<sht>>.rw_start + <<sht>>.spacing * 10
FEATURE [Part::FeaturePython] BooleanFragments002  # WARN: FeaturePython — macro-defined, semantics opaque (R4)
  Mode = 0
  Objects = -> [wrib022,wrib023,wrib024,wrib025,wrib026,wrib027,wrib028,wrib029,wrib030,wrib031,wrib032,wrib033,wrib034,wrib035,wrib036,wrib037,wrib038,wrib039,wrib040,wrib041,wrib042,wrib043,Body005,Body006]
  Tolerance = 0
FEATURE [Part::Cut] Cut
  Base = -> Box001
  Tool = -> BooleanFragments001_child0
FEATURE [Part::Cut] Cut001
  Base = -> Cut
  Tool = -> BooleanFragments001_child1
FEATURE [Part::Cut] Cut002  label="elevons"
  Base = -> BooleanFragments002
  Tool = -> Cut001
FEATURE [App::DocumentObjectGroup] GrExplode_BooleanFragments001  label="elevons001"
  Group = -> [Cut002]
FEATURE [Part::Cut] Cut003
  Base = -> BooleanFragments
  Tool = -> BooleanFragments001_child0
FEATURE [Part::Cut] Cut004  label="main body"
  Base = -> Cut003
  Tool = -> BooleanFragments001_child1
FEATURE [Part::Box] Box002  label="Cube002"
  AttacherType = Attacher::AttachEngine3D
  Height = 4.5
  Length = 9
  Placement = pos=(205,-180,-1.2) rot=(0,0,1;0rad)
  Width = 160
  expr: Height = <<sht>>.thickness
FEATURE [Part::Box] Box003  label="Cube003"
  AttacherType = Attacher::AttachEngine3D
  Height = 4.5
  Length = 9
  Placement = pos=(205,70,-1.2) rot=(0,0,1;0rad)
  Width = 160
  expr: Height = <<sht>>.thickness
FEATURE [Part::FeaturePython] Slice  # WARN: FeaturePython — macro-defined, semantics opaque (R4)
  Base = -> GrExplode_BooleanFragments001
  Mode = 1
  Tolerance = 0
  Tools = -> [Box003]
FEATURE [Part::FeaturePython] Slice_child0  label="Slice.0"  # WARN: FeaturePython — macro-defined, semantics opaque (R4)
  Base = -> Slice
  FilterType = 1
  Invert = false
  OverrideMaxVal = 0
  WindowFrom = 80
  WindowTo = 100
  items = 0
FEATURE [Part::FeaturePython] Slice001  # WARN: FeaturePython — macro-defined, semantics opaque (R4)
  Base = -> Slice_child0
  Mode = 1
  Tolerance = 0
  Tools = -> [Box002]
FEATURE [Part::FeaturePython] Slice001_child0  label="Slice001.0"  # WARN: FeaturePython — macro-defined, semantics opaque (R4)
  Base = -> Slice001
  FilterType = 1
  Invert = false
  OverrideMaxVal = 0
  WindowFrom = 80
  WindowTo = 100
  items = 0
FEATURE [Part::FeaturePython] Slice001_child1  label="Slice001.1"  # WARN: FeaturePython — macro-defined, semantics opaque (R4)
  Base = -> Slice001
  FilterType = 1
  Invert = false
  OverrideMaxVal = 0
  WindowFrom = 80
  WindowTo = 100
  items = 1
FEATURE [Part::FeaturePython] Slice001_child2  label="Slice001.2"  # WARN: FeaturePython — macro-defined, semantics opaque (R4)
  Base = -> Slice001
  FilterType = 1
  Invert = false
  OverrideMaxVal = 0
  WindowFrom = 80
  WindowTo = 100
  items = 2
FEATURE [Part::FeaturePython] Slice001_child3  label="Slice001.3"  # WARN: FeaturePython — macro-defined, semantics opaque (R4)
  Base = -> Slice001
  FilterType = 1
  Invert = false
  OverrideMaxVal = 0
  WindowFrom = 80
  WindowTo = 100
  items = 3
FEATURE [Part::FeaturePython] Slice001_child4  label="Slice001.4"  # WARN: FeaturePython — macro-defined, semantics opaque (R4)
  Base = -> Slice001
  FilterType = 1
  Invert = false
  OverrideMaxVal = 0
  WindowFrom = 80
  WindowTo = 100
  items = 4
FEATURE [Part::FeaturePython] Slice001_child5  label="Slice001.5"  # WARN: FeaturePython — macro-defined, semantics opaque (R4)
  Base = -> Slice001
  FilterType = 1
  Invert = false
  OverrideMaxVal = 0
  WindowFrom = 80
  WindowTo = 100
  items = 5
FEATURE [Part::FeaturePython] Slice001_child6  label="Slice001.6"  # WARN: FeaturePython — macro-defined, semantics opaque (R4)
  Base = -> Slice001
  FilterType = 1
  Invert = false
  OverrideMaxVal = 0
  WindowFrom = 80
  WindowTo = 100
  items = 6
FEATURE [Part::FeaturePython] Slice001_child7  label="Slice001.7"  # WARN: FeaturePython — macro-defined, semantics opaque (R4)
  Base = -> Slice001
  FilterType = 1
  Invert = false
  OverrideMaxVal = 0
  WindowFrom = 80
  WindowTo = 100
  items = 7
FEATURE [Part::FeaturePython] Slice001_child8  label="Slice001.8"  # WARN: FeaturePython — macro-defined, semantics opaque (R4)
  Base = -> Slice001
  FilterType = 1
  Invert = false
  OverrideMaxVal = 0
  WindowFrom = 80
  WindowTo = 100
  items = 8
FEATURE [Part::FeaturePython] Slice001_child9  label="Slice001.9"  # WARN: FeaturePython — macro-defined, semantics opaque (R4)
  Base = -> Slice001
  FilterType = 1
  Invert = false
  OverrideMaxVal = 0
  WindowFrom = 80
  WindowTo = 100
  items = 9
FEATURE [Part::FeaturePython] Slice001_child10  label="Slice001.10"  # WARN: FeaturePython — macro-defined, semantics opaque (R4)
  Base = -> Slice001
  FilterType = 1
  Invert = false
  OverrideMaxVal = 0
  WindowFrom = 80
  WindowTo = 100
  items = 10
FEATURE [Part::FeaturePython] Slice001_child11  label="Slice001.11"  # WARN: FeaturePython — macro-defined, semantics opaque (R4)
  Base = -> Slice001
  FilterType = 1
  Invert = false
  OverrideMaxVal = 0
  WindowFrom = 80
  WindowTo = 100
  items = 11
FEATURE [Part::FeaturePython] Slice001_child12  label="Slice001.12"  # WARN: FeaturePython — macro-defined, semantics opaque (R4)
  Base = -> Slice001
  FilterType = 1
  Invert = false
  OverrideMaxVal = 0
  WindowFrom = 80
  WindowTo = 100
  items = 12
FEATURE [Part::FeaturePython] Slice001_child13  label="Slice001.13"  # WARN: FeaturePython — macro-defined, semantics opaque (R4)
  Base = -> Slice001
  FilterType = 1
  Invert = false
  OverrideMaxVal = 0
  WindowFrom = 80
  WindowTo = 100
  items = 13
FEATURE [Part::FeaturePython] Slice001_child14  label="Slice001.14"  # WARN: FeaturePython — macro-defined, semantics opaque (R4)
  Base = -> Slice001
  FilterType = 1
  Invert = false
  OverrideMaxVal = 0
  WindowFrom = 80
  WindowTo = 100
  items = 14
FEATURE [Part::FeaturePython] Slice001_child15  label="Slice001.15"  # WARN: FeaturePython — macro-defined, semantics opaque (R4)
  Base = -> Slice001
  FilterType = 1
  Invert = false
  OverrideMaxVal = 0
  WindowFrom = 80
  WindowTo = 100
  items = 15
FEATURE [Part::FeaturePython] Slice001_child16  label="Slice001.16"  # WARN: FeaturePython — macro-defined, semantics opaque (R4)
  Base = -> Slice001
  FilterType = 1
  Invert = false
  OverrideMaxVal = 0
  WindowFrom = 80
  WindowTo = 100
  items = 16
FEATURE [Part::FeaturePython] Slice001_child17  label="Slice001.17"  # WARN: FeaturePython — macro-defined, semantics opaque (R4)
  Base = -> Slice001
  FilterType = 1
  Invert = false
  OverrideMaxVal = 0
  WindowFrom = 80
  WindowTo = 100
  items = 17
FEATURE [Part::FeaturePython] Slice001_child18  label="Slice001.18"  # WARN: FeaturePython — macro-defined, semantics opaque (R4)
  Base = -> Slice001
  FilterType = 1
  Invert = false
  OverrideMaxVal = 0
  WindowFrom = 80
  WindowTo = 100
  items = 18
FEATURE [Part::FeaturePython] Slice001_child19  label="Slice001.19"  # WARN: FeaturePython — macro-defined, semantics opaque (R4)
  Base = -> Slice001
  FilterType = 1
  Invert = false
  OverrideMaxVal = 0
  WindowFrom = 80
  WindowTo = 100
  items = 19
FEATURE [Part::FeaturePython] Slice001_child20  label="Slice001.20"  # WARN: FeaturePython — macro-defined, semantics opaque (R4)
  Base = -> Slice001
  FilterType = 1
  Invert = false
  OverrideMaxVal = 0
  WindowFrom = 80
  WindowTo = 100
  items = 20
FEATURE [Part::FeaturePython] Slice001_child21  label="Slice001.21"  # WARN: FeaturePython — macro-defined, semantics opaque (R4)
  Base = -> Slice001
  FilterType = 1
  Invert = false
  OverrideMaxVal = 0
  WindowFrom = 80
  WindowTo = 100
  items = 21
FEATURE [Part::FeaturePython] Slice001_child22  label="Slice001.22"  # WARN: FeaturePython — macro-defined, semantics opaque (R4)
  Base = -> Slice001
  FilterType = 1
  Invert = false
  OverrideMaxVal = 0
  WindowFrom = 80
  WindowTo = 100
  items = 22
FEATURE [Part::FeaturePython] Slice001_child23  label="Slice001.23"  # WARN: FeaturePython — macro-defined, semantics opaque (R4)
  Base = -> Slice001
  FilterType = 1
  Invert = false
  OverrideMaxVal = 0
  WindowFrom = 80
  WindowTo = 100
  items = 23
FEATURE [Part::FeaturePython] Slice001_child24  label="Slice001.24"  # WARN: FeaturePython — macro-defined, semantics opaque (R4)
  Base = -> Slice001
  FilterType = 1
  Invert = false
  OverrideMaxVal = 0
  WindowFrom = 80
  WindowTo = 100
  items = 24
FEATURE [Part::FeaturePython] Slice001_child25  label="Slice001.25"  # WARN: FeaturePython — macro-defined, semantics opaque (R4)
  Base = -> Slice001
  FilterType = 1
  Invert = false
  OverrideMaxVal = 0
  WindowFrom = 80
  WindowTo = 100
  items = 25
FEATURE [Part::FeaturePython] Slice001_child26  label="Slice001.26"  # WARN: FeaturePython — macro-defined, semantics opaque (R4)
  Base = -> Slice001
  FilterType = 1
  Invert = false
  OverrideMaxVal = 0
  WindowFrom = 80
  WindowTo = 100
  items = 26
FEATURE [Part::FeaturePython] Slice001_child27  label="Slice001.27"  # WARN: FeaturePython — macro-defined, semantics opaque (R4)
  Base = -> Slice001
  FilterType = 1
  Invert = false
  OverrideMaxVal = 0
  WindowFrom = 80
  WindowTo = 100
  items = 27
FEATURE [App::DocumentObjectGroup] GrExplode_Slice001  label="Exploded Slice001"
  Group = -> [Slice001_child0,Slice001_child1,Slice001_child2,Slice001_child3,Slice001_child4,Slice001_child5,Slice001_child6,Slice001_child7,Slice001_child8,Slice001_child9,Slice001_child10,Slice001_child11,Slice001_child12,Slice001_child13,Slice001_child14,Slice001_child15,Slice001_child16,Slice001_child17,Slice001_child18,Slice001_child19,Slice001_child20,Slice001_child21,Slice001_child22,Slice001_child23,+4 more]
FEATURE [Part::Box] Box004  label="Cube004"
  AttacherType = Attacher::AttachEngine3D
  Height = 4.5
  Length = 25
  Placement = pos=(157.8,-201.9,0) rot=(0,0,1;0rad)
  Width = 250
  expr: Height = <<sht>>.thickness
FEATURE [Part::Box] Box005  label="Cube005"
  AttacherType = Attacher::AttachEngine3D
  Height = 4.5
  Length = 25
  Placement = pos=(157.8,33.9,0) rot=(0,0,1;0rad)
  Width = 216
  expr: Height = <<sht>>.thickness
FEATURE [Part::Cut] Cut005
  Base = -> Cut004
  Tool = -> Body003
FEATURE [Part::Cut] Cut006
  Base = -> Cut005
  Tool = -> Body002
FEATURE [Part::Cut] Cut007
  Base = -> Cut006
  Tool = -> Box004
FEATURE [Part::Cut] Cut008
  Base = -> Cut007
  Tool = -> Box005
FEATURE [Part::FeaturePython] Cut008_child0  label="Cut008.0"  # WARN: FeaturePython — macro-defined, semantics opaque (R4)
  Base = -> Cut008
  FilterType = 1
  Invert = false
  OverrideMaxVal = 0
  WindowFrom = 80
  WindowTo = 100
  items = 0
FEATURE [Part::FeaturePython] Cut008_child1  label="Cut008.1"  # WARN: FeaturePython — macro-defined, semantics opaque (R4)
  Base = -> Cut008
  FilterType = 1
  Invert = false
  OverrideMaxVal = 0
  WindowFrom = 80
  WindowTo = 100
  items = 1
FEATURE [Part::FeaturePython] Cut008_child2  label="Cut008.2"  # WARN: FeaturePython — macro-defined, semantics opaque (R4)
  Base = -> Cut008
  FilterType = 1
  Invert = false
  OverrideMaxVal = 0
  WindowFrom = 80
  WindowTo = 100
  items = 2
FEATURE [Part::FeaturePython] Cut008_child3  label="Cut008.3"  # WARN: FeaturePython — macro-defined, semantics opaque (R4)
  Base = -> Cut008
  FilterType = 1
  Invert = false
  OverrideMaxVal = 0
  WindowFrom = 80
  WindowTo = 100
  items = 3
FEATURE [Part::FeaturePython] Cut008_child4  label="Cut008.4"  # WARN: FeaturePython — macro-defined, semantics opaque (R4)
  Base = -> Cut008
  FilterType = 1
  Invert = false
  OverrideMaxVal = 0
  WindowFrom = 80
  WindowTo = 100
  items = 4
FEATURE [Part::FeaturePython] Cut008_child5  label="Cut008.5"  # WARN: FeaturePython — macro-defined, semantics opaque (R4)
  Base = -> Cut008
  FilterType = 1
  Invert = false
  OverrideMaxVal = 0
  WindowFrom = 80
  WindowTo = 100
  items = 5
FEATURE [Part::FeaturePython] Cut008_child6  label="Cut008.6"  # WARN: FeaturePython — macro-defined, semantics opaque (R4)
  Base = -> Cut008
  FilterType = 1
  Invert = false
  OverrideMaxVal = 0
  WindowFrom = 80
  WindowTo = 100
  items = 6
FEATURE [Part::FeaturePython] Cut008_child7  label="Cut008.7"  # WARN: FeaturePython — macro-defined, semantics opaque (R4)
  Base = -> Cut008
  FilterType = 1
  Invert = false
  OverrideMaxVal = 0
  WindowFrom = 80
  WindowTo = 100
  items = 7
FEATURE [Part::FeaturePython] Cut008_child8  label="Cut008.8"  # WARN: FeaturePython — macro-defined, semantics opaque (R4)
  Base = -> Cut008
  FilterType = 1
  Invert = false
  OverrideMaxVal = 0
  WindowFrom = 80
  WindowTo = 100
  items = 8
FEATURE [Part::FeaturePython] Cut008_child9  label="Cut008.9"  # WARN: FeaturePython — macro-defined, semantics opaque (R4)
  Base = -> Cut008
  FilterType = 1
  Invert = false
  OverrideMaxVal = 0
  WindowFrom = 80
  WindowTo = 100
  items = 9
FEATURE [Part::FeaturePython] Cut008_child10  label="Cut008.10"  # WARN: FeaturePython — macro-defined, semantics opaque (R4)
  Base = -> Cut008
  FilterType = 1
  Invert = false
  OverrideMaxVal = 0
  WindowFrom = 80
  WindowTo = 100
  items = 10
FEATURE [Part::FeaturePython] Cut008_child11  label="Cut008.11"  # WARN: FeaturePython — macro-defined, semantics opaque (R4)
  Base = -> Cut008
  FilterType = 1
  Invert = false
  OverrideMaxVal = 0
  WindowFrom = 80
  WindowTo = 100
  items = 11
FEATURE [Part::FeaturePython] Cut008_child12  label="Cut008.12"  # WARN: FeaturePython — macro-defined, semantics opaque (R4)
  Base = -> Cut008
  FilterType = 1
  Invert = false
  OverrideMaxVal = 0
  WindowFrom = 80
  WindowTo = 100
  items = 12
FEATURE [Part::FeaturePython] Cut008_child13  label="Cut008.13"  # WARN: FeaturePython — macro-defined, semantics opaque (R4)
  Base = -> Cut008
  FilterType = 1
  Invert = false
  OverrideMaxVal = 0
  WindowFrom = 80
  WindowTo = 100
  items = 13
FEATURE [Part::FeaturePython] Cut008_child14  label="Cut008.14"  # WARN: FeaturePython — macro-defined, semantics opaque (R4)
  Base = -> Cut008
  FilterType = 1
  Invert = false
  OverrideMaxVal = 0
  WindowFrom = 80
  WindowTo = 100
  items = 14
FEATURE [Part::FeaturePython] Cut008_child15  label="Cut008.15"  # WARN: FeaturePython — macro-defined, semantics opaque (R4)
  Base = -> Cut008
  FilterType = 1
  Invert = false
  OverrideMaxVal = 0
  WindowFrom = 80
  WindowTo = 100
  items = 15
FEATURE [Part::FeaturePython] Cut008_child16  label="Cut008.16"  # WARN: FeaturePython — macro-defined, semantics opaque (R4)
  Base = -> Cut008
  FilterType = 1
  Invert = false
  OverrideMaxVal = 0
  WindowFrom = 80
  WindowTo = 100
  items = 16
FEATURE [Part::FeaturePython] Cut008_child17  label="Cut008.17"  # WARN: FeaturePython — macro-defined, semantics opaque (R4)
  Base = -> Cut008
  FilterType = 1
  Invert = false
  OverrideMaxVal = 0
  WindowFrom = 80
  WindowTo = 100
  items = 17
FEATURE [Part::FeaturePython] Cut008_child18  label="Cut008.18"  # WARN: FeaturePython — macro-defined, semantics opaque (R4)
  Base = -> Cut008
  FilterType = 1
  Invert = false
  OverrideMaxVal = 0
  WindowFrom = 80
  WindowTo = 100
  items = 18
FEATURE [Part::FeaturePython] Cut008_child19  label="Cut008.19"  # WARN: FeaturePython — macro-defined, semantics opaque (R4)
  Base = -> Cut008
  FilterType = 1
  Invert = false
  OverrideMaxVal = 0
  WindowFrom = 80
  WindowTo = 100
  items = 19
FEATURE [Part::FeaturePython] Cut008_child20  label="Cut008.20"  # WARN: FeaturePython — macro-defined, semantics opaque (R4)
  Base = -> Cut008
  FilterType = 1
  Invert = false
  OverrideMaxVal = 0
  WindowFrom = 80
  WindowTo = 100
  items = 20
FEATURE [Part::FeaturePython] Cut008_child21  label="Cut008.21"  # WARN: FeaturePython — macro-defined, semantics opaque (R4)
  Base = -> Cut008
  FilterType = 1
  Invert = false
  OverrideMaxVal = 0
  WindowFrom = 80
  WindowTo = 100
  items = 21
FEATURE [Part::FeaturePython] Cut008_child22  label="Cut008.22"  # WARN: FeaturePython — macro-defined, semantics opaque (R4)
  Base = -> Cut008
  FilterType = 1
  Invert = false
  OverrideMaxVal = 0
  WindowFrom = 80
  WindowTo = 100
  items = 22
FEATURE [Part::FeaturePython] Cut008_child23  label="Cut008.23"  # WARN: FeaturePython — macro-defined, semantics opaque (R4)
  Base = -> Cut008
  FilterType = 1
  Invert = false
  OverrideMaxVal = 0
  WindowFrom = 80
  WindowTo = 100
  items = 23
FEATURE [Part::FeaturePython] Cut008_child24  label="Cut008.24"  # WARN: FeaturePython — macro-defined, semantics opaque (R4)
  Base = -> Cut008
  FilterType = 1
  Invert = false
  OverrideMaxVal = 0
  WindowFrom = 80
  WindowTo = 100
  items = 24
FEATURE [Part::FeaturePython] Cut008_child25  label="Cut008.25"  # WARN: FeaturePython — macro-defined, semantics opaque (R4)
  Base = -> Cut008
  FilterType = 1
  Invert = false
  OverrideMaxVal = 0
  WindowFrom = 80
  WindowTo = 100
  items = 25
FEATURE [Part::FeaturePython] Cut008_child26  label="Cut008.26"  # WARN: FeaturePython — macro-defined, semantics opaque (R4)
  Base = -> Cut008
  FilterType = 1
  Invert = false
  OverrideMaxVal = 0
  WindowFrom = 80
  WindowTo = 100
  items = 26
FEATURE [Part::FeaturePython] Cut008_child27  label="Cut008.27"  # WARN: FeaturePython — macro-defined, semantics opaque (R4)
  Base = -> Cut008
  FilterType = 1
  Invert = false
  OverrideMaxVal = 0
  WindowFrom = 80
  WindowTo = 100
  items = 27
FEATURE [Part::FeaturePython] Cut008_child28  label="Cut008.28"  # WARN: FeaturePython — macro-defined, semantics opaque (R4)
  Base = -> Cut008
  FilterType = 1
  Invert = false
  OverrideMaxVal = 0
  WindowFrom = 80
  WindowTo = 100
  items = 28
FEATURE [Part::FeaturePython] Cut008_child29  label="Cut008.29"  # WARN: FeaturePython — macro-defined, semantics opaque (R4)
  Base = -> Cut008
  FilterType = 1
  Invert = false
  OverrideMaxVal = 0
  WindowFrom = 80
  WindowTo = 100
  items = 29
FEATURE [App::DocumentObjectGroup] GrExplode_Cut008  label="Exploded Cut008"
  Group = -> [Cut008_child0,Cut008_child1,Cut008_child2,Cut008_child3,Cut008_child4,Cut008_child5,Cut008_child6,Cut008_child7,Cut008_child8,Cut008_child9,Cut008_child10,Cut008_child11,Cut008_child12,Cut008_child13,Cut008_child14,Cut008_child15,Cut008_child16,Cut008_child17,Cut008_child18,Cut008_child19,Cut008_child20,Cut008_child21,Cut008_child22,Cut008_child23,Cut008_child24,Cut008_child25,Cut008_child26,+3 more]
FEATURE [Part::Box] Box006  label="Cube006"
  AttacherType = Attacher::AttachEngine3D
  Height = 4.5
  Length = 220
  Placement = pos=(20.4128,0,-10.7015) rot=(0,-1,0;0.034907rad)
  Width = 50
  expr: Height = <<sht>>.thickness
FEATURE [Part::Box] Box007  label="Cube007"
  AttacherType = Attacher::AttachEngine3D
  Height = 4.5
  Length = 150
  Placement = pos=(79.4043,0,14.599) rot=(0,1,0;0.087266rad)
  Width = 50
  expr: Height = <<sht>>.thickness
FEATURE [Part::Box] Box008  label="Cube008"
  AttacherType = Attacher::AttachEngine3D
  Height = 4.5
  Length = 65
  Placement = pos=(17.0091,0,-4.02296) rot=(0,-1,0;0.279253rad)
  Width = 50
  expr: Height = <<sht>>.thickness
FEATURE [App::FeaturePython] WPProxy  # WARN: FeaturePython — macro-defined, semantics opaque (R4)
  Placement = pos=(-137,-155,0) rot=(0.998836,-0.018791,-0.04443;0rad)
FEATURE [Part::Part2DObjectPython] Shape2DView  # Draft 2D object (typed FeaturePython)
  AutoUpdate = true
  Base = -> Cut008_child29
  Clip = false
  FuseArch = false
  HiddenLines = false
  InPlace = true
  OnlySolids = false
  Placement = pos=(-283,327,0) rot=(0,0,1;-1.5708rad)
  Projection = (2.06041e-09,-1,8.42937e-08)
  ProjectionMode = 0
  SegmentLength = 0.05
  Tessellation = false
  VisibleOnly = false
FEATURE [Part::Part2DObjectPython] Shape2DView001  # Draft 2D object (typed FeaturePython)
  AutoUpdate = true
  Base = -> Cut008_child18
  Clip = false
  FuseArch = false
  HiddenLines = false
  InPlace = true
  OnlySolids = false
  Placement = pos=(-108.4,0,0) rot=(0,0,1;0rad)
  Projection = (2.06041e-09,-1,8.42937e-08)
  ProjectionMode = 0
  SegmentLength = 0.05
  Tessellation = false
  VisibleOnly = false
FEATURE [Part::Part2DObjectPython] Shape2DView002  # Draft 2D object (typed FeaturePython)
  AutoUpdate = true
  Base = -> Cut008_child18
  Clip = false
  FuseArch = false
  HiddenLines = false
  InPlace = true
  OnlySolids = false
  Placement = pos=(-69.7,0,0) rot=(0,0,1;0rad)
  Projection = (1.90523e-08,-1,-8.42937e-08)
  ProjectionMode = 0
  SegmentLength = 0.05
  Tessellation = false
  VisibleOnly = false
FEATURE [Part::Part2DObjectPython] Shape2DView003  # Draft 2D object (typed FeaturePython)
  AutoUpdate = true
  Base = -> Cut008_child18
  Clip = false
  FuseArch = false
  HiddenLines = false
  InPlace = true
  OnlySolids = false
  Placement = pos=(-137.552,-1.75125,0.000151869) rot=(-1e-06,0,-1;1.55225rad)
  Projection = (4.30007e-09,-1,-2.4e-15)
  ProjectionMode = 0
  SegmentLength = 0.05
  Tessellation = false
  VisibleOnly = false
FEATURE [Part::Part2DObjectPython] Shape2DView004  # Draft 2D object (typed FeaturePython)
  AutoUpdate = true
  Base = -> Cut008_child18
  Clip = false
  FuseArch = false
  HiddenLines = false
  InPlace = true
  OnlySolids = false
  Placement = pos=(-166.107,7.22129,-8.02163) rot=(0,0,1;0rad)
  Projection = (1.87451e-09,-1,8.42937e-08)
  ProjectionMode = 0
  SegmentLength = 0.05
  Tessellation = false
  VisibleOnly = false
FEATURE [Part::Part2DObjectPython] Shape2DView005  # Draft 2D object (typed FeaturePython)
  AutoUpdate = true
  Base = -> Cut008_child17
  Clip = false
  FuseArch = false
  HiddenLines = false
  InPlace = true
  OnlySolids = false
  Placement = pos=(-170.49,-163.478,-10.1119) rot=(0,0,1;0rad)
  Projection = (9.54548e-10,-1,-8.42937e-08)
  ProjectionMode = 0
  SegmentLength = 0.05
  Tessellation = false
  VisibleOnly = false
FEATURE [Part::Part2DObjectPython] Shape2DView006  # Draft 2D object (typed FeaturePython)
  AutoUpdate = true
  Base = -> Slice001_child26
  Clip = false
  FuseArch = false
  HiddenLines = false
  InPlace = true
  OnlySolids = false
  Placement = pos=(-170.62,-168.24,0) rot=(0,0,1;0rad)
  Projection = (-3.09962e-09,-1,8.42937e-08)
  ProjectionMode = 0
  SegmentLength = 0.05
  Tessellation = false
  VisibleOnly = false
FEATURE [Part::Part2DObjectPython] Shape2DView007  # Draft 2D object (typed FeaturePython)
  AutoUpdate = true
  Base = -> Slice001_child26
  Clip = false
  FuseArch = false
  HiddenLines = false
  InPlace = true
  OnlySolids = false
  Placement = pos=(-138,-169,0) rot=(0,0,1;0rad)
  Projection = (-6.28064e-09,-1,8.42937e-08)
  ProjectionMode = 0
  SegmentLength = 0.05
  Tessellation = false
  VisibleOnly = false
FEATURE [Part::Part2DObjectPython] Shape2DView008  # Draft 2D object (typed FeaturePython)
  AutoUpdate = true
  Base = -> Cut008_child17
  Clip = false
  FuseArch = false
  HiddenLines = false
  InPlace = true
  OnlySolids = false
  Placement = pos=(-138.7,-175.03,0) rot=(0,0,1;0rad)
  Projection = (-6.28064e-09,-1,8.42937e-08)
  ProjectionMode = 0
  SegmentLength = 0.05
  Tessellation = false
  VisibleOnly = false
FEATURE [Part::Part2DObjectPython] Shape2DView009  # Draft 2D object (typed FeaturePython)
  AutoUpdate = true
  Base = -> Slice001_child20
  Clip = false
  FuseArch = false
  HiddenLines = false
  InPlace = true
  OnlySolids = false
  Placement = pos=(-102.28,-181.94,0) rot=(0,0,1;0rad)
  Projection = (-4.9983e-09,-1,8.42937e-08)
  ProjectionMode = 0
  SegmentLength = 0.05
  Tessellation = false
  VisibleOnly = false
FEATURE [Part::Part2DObjectPython] Shape2DView010  # Draft 2D object (typed FeaturePython)
  AutoUpdate = true
  Base = -> Cut008_child14
  Clip = false
  FuseArch = false
  HiddenLines = false
  InPlace = true
  OnlySolids = false
  Placement = pos=(-102.28,-181.94,0) rot=(0,0,1;0rad)
  Projection = (-4.9983e-09,-1,8.42937e-08)
  ProjectionMode = 0
  SegmentLength = 0.05
  Tessellation = false
  VisibleOnly = false
FEATURE [Part::Part2DObjectPython] Shape2DView011  # Draft 2D object (typed FeaturePython)
  AutoUpdate = true
  Base = -> Slice001_child20
  Clip = false
  FuseArch = false
  HiddenLines = false
  InPlace = true
  OnlySolids = false
  Placement = pos=(-68,-165,0) rot=(0,0,1;-1.5708rad)
  Projection = (-1.36339e-10,-1,-3e-16)
  ProjectionMode = 0
  SegmentLength = 0.05
  Tessellation = false
  VisibleOnly = false
FEATURE [Part::Part2DObjectPython] Shape2DView012  # Draft 2D object (typed FeaturePython)
  AutoUpdate = true
  Base = -> Cut008_child14
  Clip = false
  FuseArch = false
  HiddenLines = false
  InPlace = true
  OnlySolids = false
  Placement = pos=(-68,-165,0) rot=(0,0,1;-1.5708rad)
  Projection = (-1.36339e-10,-1,-3e-16)
  ProjectionMode = 0
  SegmentLength = 0.05
  Tessellation = false
  VisibleOnly = false
FEATURE [Part::Part2DObjectPython] Shape2DView013  # Draft 2D object (typed FeaturePython)
  AutoUpdate = true
  Base = -> Slice001_child20
  Clip = false
  FuseArch = false
  HiddenLines = false
  InPlace = true
  OnlySolids = false
  Placement = pos=(-34,-183,0) rot=(0,0,1;0rad)
  Projection = (-6.43613e-09,-1,8.42937e-08)
  ProjectionMode = 0
  SegmentLength = 0.05
  Tessellation = false
  VisibleOnly = false
FEATURE [Part::Part2DObjectPython] Shape2DView014  # Draft 2D object (typed FeaturePython)
  AutoUpdate = true
  Base = -> Cut008_child14
  Clip = false
  FuseArch = false
  HiddenLines = false
  InPlace = true
  OnlySolids = false
  Placement = pos=(-34,-183,0) rot=(0,0,1;0rad)
  Projection = (-6.43613e-09,-1,8.42937e-08)
  ProjectionMode = 0
  SegmentLength = 0.05
  Tessellation = false
  VisibleOnly = false
FEATURE [Part::Part2DObjectPython] Shape2DView015  # Draft 2D object (typed FeaturePython)
  AutoUpdate = true
  Base = -> Slice001_child14
  Clip = false
  FuseArch = false
  HiddenLines = false
  InPlace = true
  OnlySolids = false
  Placement = pos=(-33,21,0) rot=(0,0,1;0rad)
  Projection = (2.10734e-08,-1,-8.42937e-08)
  ProjectionMode = 0
  SegmentLength = 0.05
  Tessellation = false
  VisibleOnly = false
FEATURE [Part::Part2DObjectPython] Shape2DView016  # Draft 2D object (typed FeaturePython)
  AutoUpdate = true
  Base = -> Cut008_child11
  Clip = false
  FuseArch = false
  HiddenLines = false
  InPlace = true
  OnlySolids = false
  Placement = pos=(-33,21,0) rot=(0,0,1;0rad)
  Projection = (2.10734e-08,-1,-8.42937e-08)
  ProjectionMode = 0
  SegmentLength = 0.05
  Tessellation = false
  VisibleOnly = false
FEATURE [Part::Part2DObjectPython] Shape2DView017  # Draft 2D object (typed FeaturePython)
  AutoUpdate = true
  Base = -> Cut008_child11
  Clip = false
  FuseArch = false
  HiddenLines = false
  InPlace = true
  OnlySolids = false
  Placement = pos=(-203.26,-141,0) rot=(0,0,1;4.71239rad)
  Projection = (-1.27042e-09,-1,4e-16)
  ProjectionMode = 0
  SegmentLength = 0.05
  Tessellation = false
  VisibleOnly = false
FEATURE [Part::Part2DObjectPython] Shape2DView018  # Draft 2D object (typed FeaturePython)
  AutoUpdate = true
  Base = -> Slice001_child14
  Clip = false
  FuseArch = false
  HiddenLines = false
  InPlace = true
  OnlySolids = false
  Placement = pos=(-203.26,-141,0) rot=(0,0,1;4.71239rad)
  Projection = (-1.27042e-09,-1,4e-16)
  ProjectionMode = 0
  SegmentLength = 0.05
  Tessellation = false
  VisibleOnly = false
FEATURE [Part::Part2DObjectPython] Shape2DView019  # Draft 2D object (typed FeaturePython)
  AutoUpdate = true
  Base = -> Cut008_child10
  Clip = false
  FuseArch = false
  HiddenLines = false
  InPlace = true
  OnlySolids = false
  Placement = pos=(2,37,0) rot=(0,0,1;0rad)
  Projection = (-2.2943e-12,-1,-8.42937e-08)
  ProjectionMode = 0
  SegmentLength = 0.05
  Tessellation = false
  VisibleOnly = false
FEATURE [Part::Part2DObjectPython] Shape2DView020  # Draft 2D object (typed FeaturePython)
  AutoUpdate = true
  Base = -> Slice001_child12
  Clip = false
  FuseArch = false
  HiddenLines = false
  InPlace = true
  OnlySolids = false
  Placement = pos=(2,37,0) rot=(0,0,1;0rad)
  Projection = (-2.2943e-12,-1,-8.42937e-08)
  ProjectionMode = 0
  SegmentLength = 0.05
  Tessellation = false
  VisibleOnly = false
FEATURE [App::MeasureDistance] Distance  label="Distance: 453.70 mm"
  Distance = 453.703
  P1 = (241.562,250,32.3877)
  P2 = (240.062,-203.7,31.9889)
FEATURE [Sketcher::SketchObject] Sketch003
  AttachmentOffset = pos=(0,0,207) rot=(0,0,1;0rad)
  FullyConstrained = false
  MapMode = 5
  Placement = pos=(0,-207,4.6e-14) rot=(1,0,0;1.5708rad)
  Support = -> [XZ_Plane007]
  sketch-geometry (15):
    g0-g7: Circle x8 (B-spline internal-alignment scaffolding for g8; pole/knot coordinates omitted)
    g8: BSplineCurve PolesCount=8 KnotsCount=6 Degree=3 IsPeriodic=0
    g9-g14: GeomPoint x6 (B-spline internal-alignment scaffolding for g8; pole/knot coordinates omitted)
  constraints (4):
    c: Weight(g0) = 1
    c: Equal(g0, g1-g7) x7
    c: InternalAlignment(g0-g7 -> g8) x8
    c: InternalAlignment(g9-g14 -> g8) x6
FEATURE [Sketcher::SketchObject] Sketch005
  AttachmentOffset = pos=(0,0,40) rot=(0,0,1;0rad)
  FullyConstrained = false
  MapMode = 5
  Placement = pos=(0,-40,8.9e-15) rot=(1,0,0;1.5708rad)
  Support = -> [XZ_Plane007]
  sketch-geometry (19):
    g0-g9: Circle x10 (B-spline internal-alignment scaffolding for g10; pole/knot coordinates omitted)
    g10: BSplineCurve PolesCount=10 KnotsCount=8 Degree=3 IsPeriodic=0
    g11-g18: GeomPoint x8 (B-spline internal-alignment scaffolding for g10; pole/knot coordinates omitted)
  constraints (4):
    c: Weight(g0) = 1
    c: Equal(g0, g1-g9) x9
    c: InternalAlignment(g0-g9 -> g10) x10
    c: InternalAlignment(g11-g18 -> g10) x8
FEATURE [Sketcher::SketchObject] Sketch004
  AttachmentOffset = pos=(0,0,186) rot=(0,0,1;0rad)
  FullyConstrained = false
  Placement = pos=(0,-160,4.13e-14) rot=(1,0,0;1.5708rad)
  sketch-geometry (15):
    g0-g7: Circle x8 (B-spline internal-alignment scaffolding for g8; pole/knot coordinates omitted)
    g8: BSplineCurve PolesCount=8 KnotsCount=6 Degree=3 IsPeriodic=0
    g9-g14: GeomPoint x6 (B-spline internal-alignment scaffolding for g8; pole/knot coordinates omitted)
  constraints (4):
    c: Weight(g0) = 1
    c: Equal(g0, g1-g7) x7
    c: InternalAlignment(g0-g7 -> g8) x8
    c: InternalAlignment(g9-g14 -> g8) x6
FEATURE [PartDesign::Body] Body007  label="Body"
  Group = -> [Sketch003,Sketch005,Sketch004]
  Origin = -> Origin007
FEATURE [Part::RuledSurface] Ruled_Surface
  Curve1 = -> Sketch005
  Curve2 = -> Sketch004
  Orientation = 0
FEATURE [Part::RuledSurface] Ruled_Surface001
  Curve1 = -> Sketch004
  Curve2 = -> Sketch003
  Orientation = 0
FEATURE [Part::MultiFuse] Fusion001
  Shapes = -> [Ruled_Surface,Ruled_Surface001]
FEATURE [Mesh::Feature] Mesh  label="Fusion001 (Meshed)"
FEATURE [Part::Feature] Shape
  Placement = pos=(-137,-155,0) rot=(0.998836,-0.018791,-0.04443;0rad)
  shape: bbox 206 x 91.26 x 2e-07 mm, 0 faces, 0 solids (baked)
FEATURE [Part::Part2DObjectPython] ShapeString  # Draft 2D object (typed FeaturePython)
  FontFile = /Library/Fonts/Arial Unicode.ttf
  MakeFace = true
  Placement = pos=(-172.49,-74.74,-117.47) rot=(0.783488,0.08963,-0.614909;1.04727rad)
  Size = 1
  String = wing edge r
  Tracking = 0
